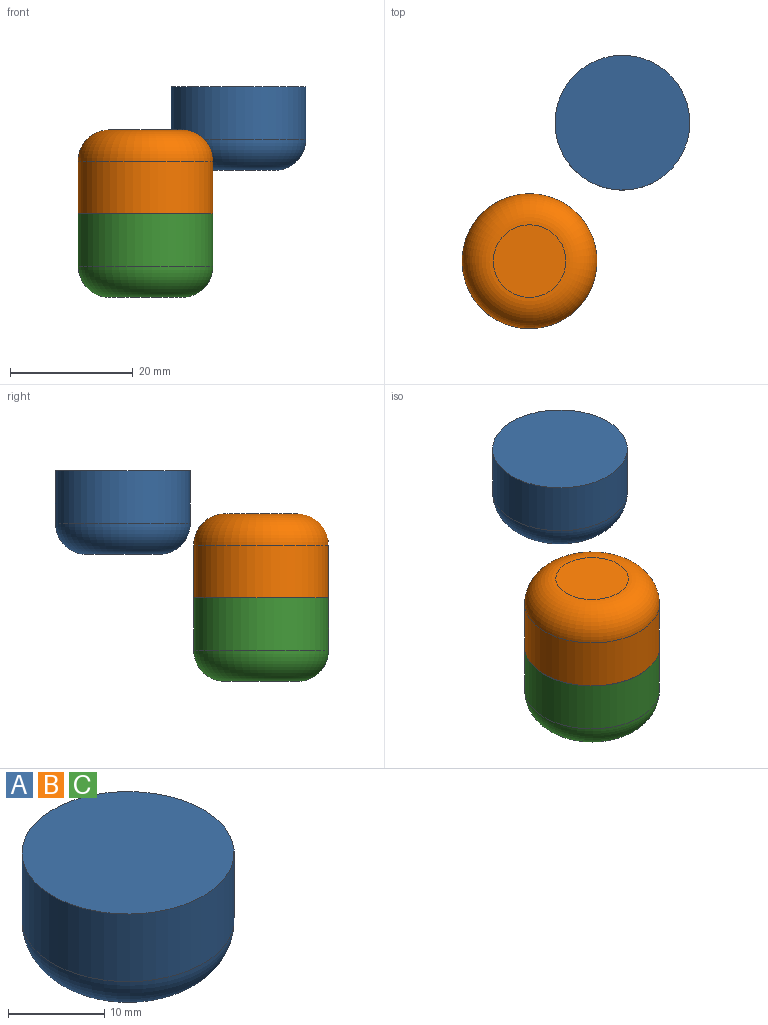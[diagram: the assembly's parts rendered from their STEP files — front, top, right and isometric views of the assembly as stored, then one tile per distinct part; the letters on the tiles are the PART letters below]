
ASSEMBLY  parts=3 mates=1
PART A: 4 faces, bbox 23.8x23.8x13.7 mm
  f0: cylinder r=11mm len=22mm, axis (0,0,-1), area 593.4mm2, adj f1,f3
  f1: plane 22x22mm, normal (0,0,1), area 380.1mm2, adj f0
  f2: plane 11.84x11.84mm, normal (0,0,-1), area 110.1mm2, adj f3
  f3: torus R=5.92mm, axis (0,0,1), area 459mm2, adj f0,f2
PART B: same geometry as A
PART C: same geometry as A
PLACE A t=(13.19,24.78,18.91)mm
PLACE B rot(axis=(0.71,0.71,0),180deg) t=(-1.97,2.21,25.51)mm
PLACE C t=(-1.97,2.21,-1.82)mm
MATE fastened B.f0 <-> C.f0  axis (0,0,-1) through (-1.97,2.21,11.85)mm
